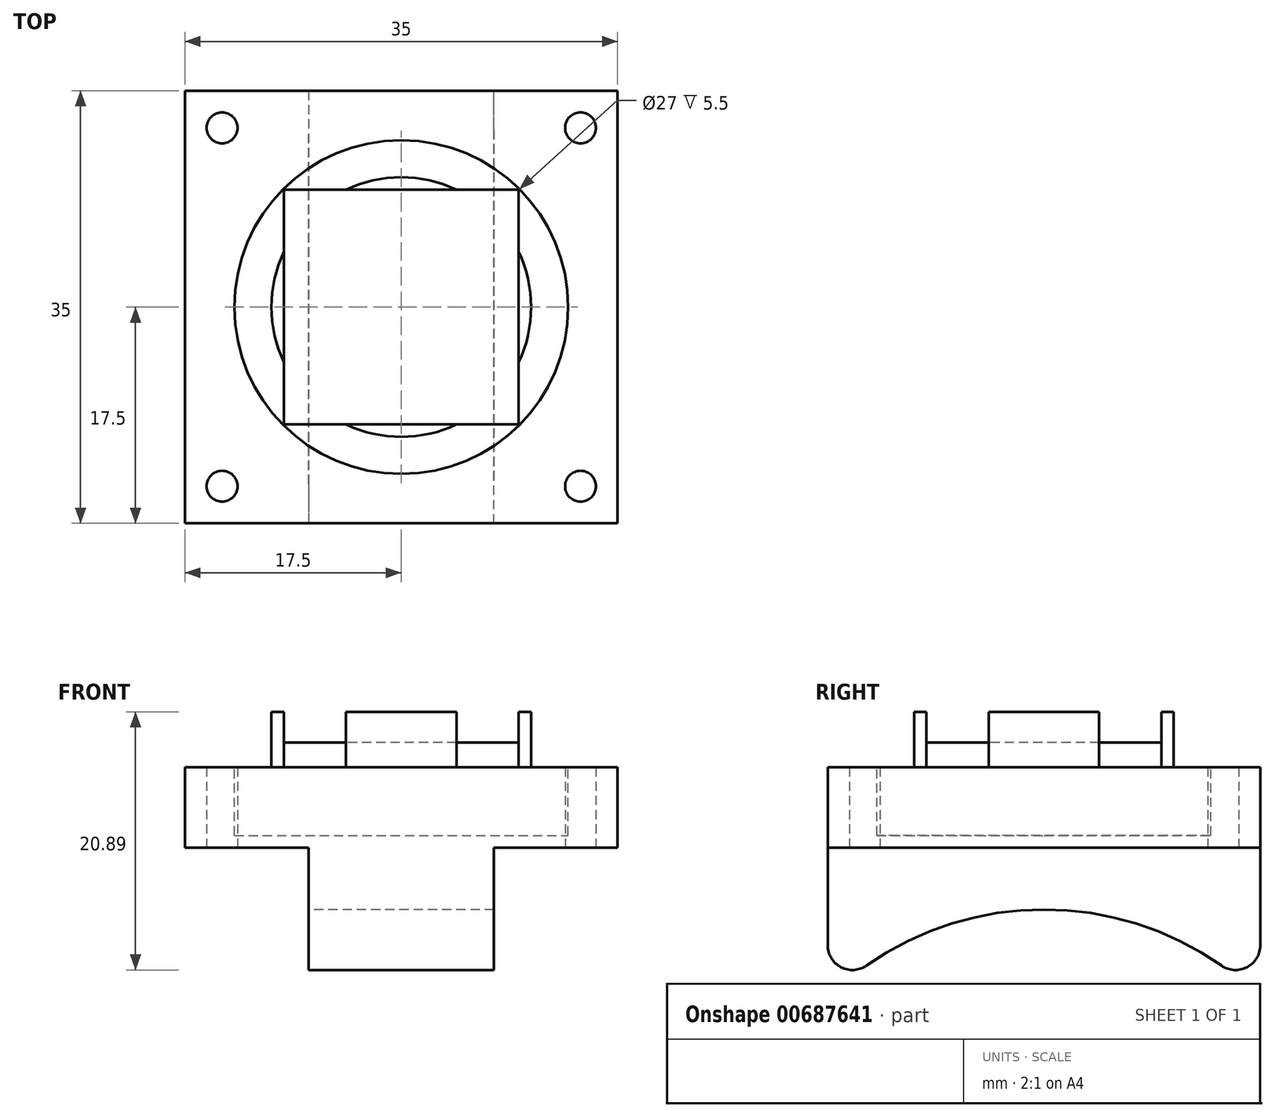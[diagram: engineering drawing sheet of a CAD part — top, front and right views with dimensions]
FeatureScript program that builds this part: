
annotation { "Feature Type Name" : "Feature", "Feature Type Description" : "" }
export const myFeature = defineFeature(function(context is Context, id is Id, definition is map)
    precondition{}
    {
        {
            var Q0;
            Q0=qCreatedBy(makeId("Top.planeOp"),FACE);
            var sketch = newSketch(context, id + "F0", { "sketchPlane" : qUnion([Q0])});
            skLineSegment(sketch, "E0", {"start": v(0, 0) * mm, "end": v(-19, 0) * mm});
            skLineSegment(sketch, "E1", {"start": v(-19, 0) * mm, "end": v(-19, 19) * mm});
            skLineSegment(sketch, "E2", {"start": v(-19, 19) * mm, "end": v(0, 19) * mm});
            skLineSegment(sketch, "E3", {"start": v(0, 19) * mm, "end": v(0, 0) * mm});
            skLineSegment(sketch, "E4.0", {"start": v(2, -2) * mm, "end": v(-21, -2) * mm});
            skLineSegment(sketch, "E4.1", {"start": v(2, 21) * mm, "end": v(2, -2) * mm});
            skLineSegment(sketch, "E4.2", {"start": v(-21, 21) * mm, "end": v(2, 21) * mm});
            skLineSegment(sketch, "E4.3", {"start": v(-21, -2) * mm, "end": v(-21, 21) * mm});
            skCircle(sketch, "E5", {"center": v(-9.5, 9.5) * mm, "radius": 10.5 * mm});
            skPoint(sketch, "E5.centerSnap0", {"position": v(-9.5, 0) * mm});
            skPoint(sketch, "E5.centerSnap1", {"position": v(0, 9.5) * mm});
            skLineSegment(sketch, "E6.0", {"start": v(8, -8) * mm, "end": v(-27, -8) * mm});
            skLineSegment(sketch, "E6.1", {"start": v(8, 27) * mm, "end": v(8, -8) * mm});
            skLineSegment(sketch, "E6.2", {"start": v(-27, 27) * mm, "end": v(8, 27) * mm});
            skLineSegment(sketch, "E6.3", {"start": v(-27, -8) * mm, "end": v(-27, 27) * mm});
            skLineSegment(sketch, "E7", {"start": v(-27, -8) * mm, "end": v(-21, -2) * mm});
            skLineSegment(sketch, "E8", {"start": v(-27, -8) * mm, "end": v(-24, -5) * mm});
            skLineSegment(sketch, "E9", {"start": v(-9.5, 9.5) * mm, "end": v(-11.5, 9.5) * mm});
            skLineSegment(sketch, "E10", {"start": v(-9.5, 9.5) * mm, "end": v(-9.5, 11.53) * mm});
            skLineSegment(sketch, "E11.MirrorCS", {"start": v(-27, 27) * mm, "end": v(-24, 24) * mm});
            skLineSegment(sketch, "E12.MirrorCS", {"start": v(8, -8) * mm, "end": v(5, -5) * mm});
            skLineSegment(sketch, "E13.MirrorCS", {"start": v(8, 27) * mm, "end": v(5, 24) * mm});
            skSolve(sketch);
        }
        {
            var Q0;
            Q0=qSketchRegion(id+"F0",true);
            var Q1;
            {var subQ0=sQuery(id+"F0.wireOp",EDGE,"E5");var subQ1=sQuery(id+"F0.wireOp",EDGE,"E3");var subQ2=makeQuery(id+"F0.imprint","INTERSECT",VERTEX,{"disambiguationData":[OD(0.0)],"derivedFrom":[subQ1,subQ0]});Q1=makeQuery(id+"F0.imprint","IMPRINT",FACE,{"disambiguationData":[TD([[makeQuery(id+"F0.imprint","IMPRINT",EDGE,{"disambiguationData":[TD([[subQ2,-1.0]])],"derivedFrom":subQ1}),1.0]])]});}
            var Q2;
            {var subQ0=sQuery(id+"F0.wireOp",EDGE,"E5");var subQ1=sQuery(id+"F0.wireOp",EDGE,"E0");var subQ2=makeQuery(id+"F0.imprint","INTERSECT",VERTEX,{"disambiguationData":[OD(0.0)],"derivedFrom":[subQ1,subQ0]});Q2=makeQuery(id+"F0.imprint","IMPRINT",FACE,{"disambiguationData":[TD([[makeQuery(id+"F0.imprint","IMPRINT",EDGE,{"disambiguationData":[TD([[subQ2,-1.0]])],"derivedFrom":subQ1}),1.0]])]});}
            var Q3;
            {var subQ0=sQuery(id+"F0.wireOp",EDGE,"E5");var subQ1=sQuery(id+"F0.wireOp",EDGE,"E1");var subQ2=makeQuery(id+"F0.imprint","INTERSECT",VERTEX,{"disambiguationData":[OD(0.0)],"derivedFrom":[subQ1,subQ0]});Q3=makeQuery(id+"F0.imprint","IMPRINT",FACE,{"disambiguationData":[TD([[makeQuery(id+"F0.imprint","IMPRINT",EDGE,{"disambiguationData":[TD([[subQ2,-1.0]])],"derivedFrom":subQ1}),1.0]])]});}
            var Q4;
            {var subQ0=sQuery(id+"F0.wireOp",EDGE,"E5");var subQ1=sQuery(id+"F0.wireOp",EDGE,"E2");var subQ2=makeQuery(id+"F0.imprint","INTERSECT",VERTEX,{"disambiguationData":[OD(0.0)],"derivedFrom":[subQ1,subQ0]});Q4=makeQuery(id+"F0.imprint","IMPRINT",FACE,{"disambiguationData":[TD([[makeQuery(id+"F0.imprint","IMPRINT",EDGE,{"disambiguationData":[TD([[subQ2,-1.0]])],"derivedFrom":subQ1}),1.0]])]});}
            var Q5;
            {var subQ0=sQuery(id+"F0.wireOp",EDGE,"E2");var subQ1=sQuery(id+"F0.wireOp",EDGE,"E1");var subQ2=makeQuery(id+"F0.imprint","INTERSECT",VERTEX,{"derivedFrom":[subQ1,subQ0]});Q5=makeQuery(id+"F0.imprint","IMPRINT",FACE,{"disambiguationData":[TD([[makeQuery(id+"F0.imprint","IMPRINT",EDGE,{"disambiguationData":[TD([[subQ2,1.0]])],"derivedFrom":subQ1}),-1.0]])]});}
            var Q6;
            {var subQ0=sQuery(id+"F0.wireOp",EDGE,"E3");var subQ1=sQuery(id+"F0.wireOp",EDGE,"E2");var subQ2=makeQuery(id+"F0.imprint","INTERSECT",VERTEX,{"derivedFrom":[subQ1,subQ0]});Q6=makeQuery(id+"F0.imprint","IMPRINT",FACE,{"disambiguationData":[TD([[makeQuery(id+"F0.imprint","IMPRINT",EDGE,{"disambiguationData":[TD([[subQ2,1.0]])],"derivedFrom":subQ1}),-1.0]])]});}
            var Q7;
            {var subQ0=sQuery(id+"F0.wireOp",EDGE,"E3");var subQ1=sQuery(id+"F0.wireOp",EDGE,"E0");var subQ2=makeQuery(id+"F0.imprint","INTERSECT",VERTEX,{"derivedFrom":[subQ1,subQ0]});Q7=makeQuery(id+"F0.imprint","IMPRINT",FACE,{"disambiguationData":[TD([[makeQuery(id+"F0.imprint","IMPRINT",EDGE,{"disambiguationData":[TD([[subQ2,-1.0]])],"derivedFrom":subQ1}),-1.0]])]});}
            var Q8;
            {var subQ0=sQuery(id+"F0.wireOp",EDGE,"E1");var subQ1=sQuery(id+"F0.wireOp",EDGE,"E0");var subQ2=makeQuery(id+"F0.imprint","INTERSECT",VERTEX,{"derivedFrom":[subQ1,subQ0]});Q8=makeQuery(id+"F0.imprint","IMPRINT",FACE,{"disambiguationData":[TD([[makeQuery(id+"F0.imprint","IMPRINT",EDGE,{"disambiguationData":[TD([[subQ2,1.0]])],"derivedFrom":subQ1}),-1.0]])]});}
            var Q9;
            Q9=makeQuery(id+"F0.imprint","IMPRINT",FACE,{"disambiguationData":[TD([[makeQuery(id+"F0.imprint","IMPRINT",EDGE,{"derivedFrom":sQuery(id+"F0.wireOp",EDGE,"E4.0")}),-1.0]])]});
            var Q10;
            {var subQ0=sQuery(id+"F0.wireOp",EDGE,"E5");var subQ10=sQuery(id+"F0.wireOp",EDGE,"E0");var subQ11=makeQuery(id+"F0.imprint","INTERSECT",VERTEX,{"disambiguationData":[OD(0.0)],"derivedFrom":[subQ10,subQ0]});Q10=makeQuery(id+"F0.imprint","IMPRINT",FACE,{"disambiguationData":[TD([[makeQuery(id+"F0.imprint","IMPRINT",EDGE,{"disambiguationData":[TD([[subQ11,-1.0]])],"derivedFrom":subQ10}),-1.0]])]});}
            extrude(context, id + "F1", {"entities" : qUnion([Q0, Q1, Q2, Q3, Q4, Q5, Q6, Q7, Q8, Q9, Q10]), "oppositeDirection" : true, "depth" : 2 * mm, "offsetDistance" : 25 * mm});
        }
        {
            var Q0;
            Q0=makeQuery(id+"F1.opExtrude","CAP_FACE",FACE,{"disambiguationData":[OSD([sQuery(id+"F0.wireOp",EDGE,"E6.0"),sQuery(id+"F0.wireOp",EDGE,"E6.1"),sQuery(id+"F0.wireOp",EDGE,"E6.2"),sQuery(id+"F0.wireOp",EDGE,"E6.3")])],"isStart":false});
            var sketch = newSketch(context, id + "F2", { "sketchPlane" : qUnion([Q0])});
            skLineSegment(sketch, "E14", {"start": v(-27, -27) * mm, "end": v(-27, 8) * mm});
            skLineSegment(sketch, "E15", {"start": v(-27, 8) * mm, "end": v(8, 8) * mm});
            skLineSegment(sketch, "E16", {"start": v(8, 8) * mm, "end": v(8, -27) * mm});
            skLineSegment(sketch, "E17", {"start": v(8, -27) * mm, "end": v(-27, -27) * mm});
            skLineSegment(sketch, "E18", {"start": v(-27, -9.5) * mm, "end": v(8, -9.5) * mm});
            skCircle(sketch, "E19", {"center": v(-9.5, -9.5) * mm, "radius": 13.5 * mm});
            skSolve(sketch);
        }
        {
            var Q0;
            Q0=qSketchRegion(id+"F2",true);
            extrude(context, id + "F3", {"entities" : qUnion([Q0]), "depth" : 5.5 * mm, "offsetDistance" : 25 * mm});
        }
        {
            var Q0;
            {var subQ0=sQuery(id+"F0.wireOp",EDGE,"E5");var subQ1=sQuery(id+"F0.wireOp",EDGE,"E1");var subQ2=makeQuery(id+"F0.imprint","INTERSECT",VERTEX,{"disambiguationData":[OD(0.0)],"derivedFrom":[subQ1,subQ0]});Q0=makeQuery(id+"F0.imprint","IMPRINT",FACE,{"disambiguationData":[TD([[makeQuery(id+"F0.imprint","IMPRINT",EDGE,{"disambiguationData":[TD([[subQ2,-1.0]])],"derivedFrom":subQ1}),1.0]])]});}
            var Q1;
            {var subQ0=sQuery(id+"F0.wireOp",EDGE,"E5");var subQ1=sQuery(id+"F0.wireOp",EDGE,"E2");var subQ2=makeQuery(id+"F0.imprint","INTERSECT",VERTEX,{"disambiguationData":[OD(0.0)],"derivedFrom":[subQ1,subQ0]});Q1=makeQuery(id+"F0.imprint","IMPRINT",FACE,{"disambiguationData":[TD([[makeQuery(id+"F0.imprint","IMPRINT",EDGE,{"disambiguationData":[TD([[subQ2,-1.0]])],"derivedFrom":subQ1}),1.0]])]});}
            var Q2;
            {var subQ0=sQuery(id+"F0.wireOp",EDGE,"E5");var subQ1=sQuery(id+"F0.wireOp",EDGE,"E3");var subQ2=makeQuery(id+"F0.imprint","INTERSECT",VERTEX,{"disambiguationData":[OD(0.0)],"derivedFrom":[subQ1,subQ0]});Q2=makeQuery(id+"F0.imprint","IMPRINT",FACE,{"disambiguationData":[TD([[makeQuery(id+"F0.imprint","IMPRINT",EDGE,{"disambiguationData":[TD([[subQ2,-1.0]])],"derivedFrom":subQ1}),1.0]])]});}
            var Q3;
            {var subQ0=sQuery(id+"F0.wireOp",EDGE,"E5");var subQ1=sQuery(id+"F0.wireOp",EDGE,"E0");var subQ2=makeQuery(id+"F0.imprint","INTERSECT",VERTEX,{"disambiguationData":[OD(0.0)],"derivedFrom":[subQ1,subQ0]});Q3=makeQuery(id+"F0.imprint","IMPRINT",FACE,{"disambiguationData":[TD([[makeQuery(id+"F0.imprint","IMPRINT",EDGE,{"disambiguationData":[TD([[subQ2,-1.0]])],"derivedFrom":subQ1}),1.0]])]});}
            var Q4;
            Q4=makeQuery(id+"F0.imprint","IMPRINT",FACE,{"disambiguationData":[TD([[makeQuery(id+"F0.imprint","IMPRINT",EDGE,{"derivedFrom":sQuery(id+"F0.wireOp",EDGE,"E4.0")}),-1.0]])]});
            extrude(context, id + "F4", {"entities" : qUnion([Q0, Q1, Q2, Q3, Q4]), "operationType" : NewBodyOperationType.ADD, "depth" : 2.5 * mm, "offsetDistance" : 25 * mm});
        }
        {
            var Q0;
            Q0=makeQuery(id+"F3.opExtrude","CAP_FACE",FACE,{"disambiguationData":[OSD([sQuery(id+"F2.wireOp",EDGE,"E14"),sQuery(id+"F2.wireOp",EDGE,"E15"),sQuery(id+"F2.wireOp",EDGE,"E16"),sQuery(id+"F2.wireOp",EDGE,"E17"),sQuery(id+"F2.wireOp",EDGE,"E19")])],"isStart":false});
            var Q1;
            Q1=makeQuery(id+"F1.opExtrude","CAP_FACE",FACE,{"disambiguationData":[OSD([sQuery(id+"F0.wireOp",EDGE,"E6.0"),sQuery(id+"F0.wireOp",EDGE,"E6.1"),sQuery(id+"F0.wireOp",EDGE,"E6.2"),sQuery(id+"F0.wireOp",EDGE,"E6.3")])],"isStart":false});
            extrude(context, id + "F5", {"entities" : qUnion([Q0, Q1]), "depth" : 1 * mm, "offsetDistance" : 25 * mm});
        }
        {
            var Q0;
            Q0=makeQuery(id+"F5.opExtrude","SWEPT_BODY",BODY,{"disambiguationData":[OSD([sQuery(id+"F2.wireOp",EDGE,"E14"),sQuery(id+"F2.wireOp",EDGE,"E15"),sQuery(id+"F2.wireOp",EDGE,"E16"),sQuery(id+"F2.wireOp",EDGE,"E17"),sQuery(id+"F2.wireOp",EDGE,"E19")])]});
            var Q1;
            Q1=makeQuery(id+"F5.opExtrude","SWEPT_BODY",BODY,{"disambiguationData":[OSD([sQuery(id+"F0.wireOp",EDGE,"E6.0"),sQuery(id+"F0.wireOp",EDGE,"E6.1"),sQuery(id+"F0.wireOp",EDGE,"E6.2"),sQuery(id+"F0.wireOp",EDGE,"E6.3")])]});
            deleteBodies(context, id + "F6", {"entities" : qUnion([Q0, Q1])});
        }
        {
            var Q0;
            Q0=makeQuery(id+"F3.opExtrude","CAP_FACE",FACE,{"disambiguationData":[OSD([sQuery(id+"F2.wireOp",EDGE,"E14"),sQuery(id+"F2.wireOp",EDGE,"E15"),sQuery(id+"F2.wireOp",EDGE,"E16"),sQuery(id+"F2.wireOp",EDGE,"E17"),sQuery(id+"F2.wireOp",EDGE,"E19")])],"isStart":false});
            var sketch = newSketch(context, id + "F7", { "sketchPlane" : qUnion([Q0])});
            skLineSegment(sketch, "E20", {"start": v(-27, -27) * mm, "end": v(8, -27) * mm});
            skLineSegment(sketch, "E21", {"start": v(8, -27) * mm, "end": v(8, 8) * mm});
            skLineSegment(sketch, "E22", {"start": v(8, 8) * mm, "end": v(-27, 8) * mm});
            skLineSegment(sketch, "E23", {"start": v(-27, 8) * mm, "end": v(-27, -27) * mm});
            skSolve(sketch);
        }
        {
            var Q0;
            Q0=makeQuery(id+"F7.imprint","IMPRINT",FACE,{"disambiguationData":[TD([[makeQuery(id+"F7.imprint","IMPRINT",EDGE,{"derivedFrom":sQuery(id+"F7.wireOp",EDGE,"E20")}),1.0]])]});
            var Q1;
            Q1=makeQuery(id+"F7.imprint","IMPRINT",FACE,{"disambiguationData":[TD([[makeQuery(id+"F7.imprint","IMPRINT",EDGE,{"derivedFrom":makeQuery(id+"FP3SZp29wrBzVes_1.hole-0.boolean.opBoolean","INTERSECT",EDGE,{"derivedFrom":[makeQuery(id+"F3.opExtrude","CAP_FACE",FACE,{"disambiguationData":[OSD([sQuery(id+"F2.wireOp",EDGE,"E14"),sQuery(id+"F2.wireOp",EDGE,"E15"),sQuery(id+"F2.wireOp",EDGE,"E16"),sQuery(id+"F2.wireOp",EDGE,"E17"),sQuery(id+"F2.wireOp",EDGE,"E19")])],"isStart":false}),makeQuery(id+"FP3SZp29wrBzVes_1.hole-0.opRevolve","SWEPT_FACE",FACE,{"disambiguationData":[OSD([sQuery(id+"FP3SZp29wrBzVes_1.hole-0.sketch.wireOp",EDGE,"core_line_2")])]})]})}),-1.0]])]});
            var Q2;
            Q2=makeQuery(id+"F7.imprint","IMPRINT",FACE,{"disambiguationData":[TD([[makeQuery(id+"F7.imprint","IMPRINT",EDGE,{"derivedFrom":makeQuery(id+"FP3SZp29wrBzVes_1.hole-1.boolean.opBoolean","INTERSECT",EDGE,{"derivedFrom":[makeQuery(id+"F3.opExtrude","CAP_FACE",FACE,{"disambiguationData":[OSD([sQuery(id+"F2.wireOp",EDGE,"E14"),sQuery(id+"F2.wireOp",EDGE,"E15"),sQuery(id+"F2.wireOp",EDGE,"E16"),sQuery(id+"F2.wireOp",EDGE,"E17"),sQuery(id+"F2.wireOp",EDGE,"E19")])],"isStart":false}),makeQuery(id+"FP3SZp29wrBzVes_1.hole-1.opRevolve","SWEPT_FACE",FACE,{"disambiguationData":[OSD([sQuery(id+"FP3SZp29wrBzVes_1.hole-1.sketch.wireOp",EDGE,"core_line_2")])]})]})}),-1.0]])]});
            var Q3;
            Q3=makeQuery(id+"F7.imprint","IMPRINT",FACE,{"disambiguationData":[TD([[makeQuery(id+"F7.imprint","IMPRINT",EDGE,{"derivedFrom":makeQuery(id+"FP3SZp29wrBzVes_1.hole-3.boolean.opBoolean","INTERSECT",EDGE,{"derivedFrom":[makeQuery(id+"F3.opExtrude","CAP_FACE",FACE,{"disambiguationData":[OSD([sQuery(id+"F2.wireOp",EDGE,"E14"),sQuery(id+"F2.wireOp",EDGE,"E15"),sQuery(id+"F2.wireOp",EDGE,"E16"),sQuery(id+"F2.wireOp",EDGE,"E17"),sQuery(id+"F2.wireOp",EDGE,"E19")])],"isStart":false}),makeQuery(id+"FP3SZp29wrBzVes_1.hole-3.opRevolve","SWEPT_FACE",FACE,{"disambiguationData":[OSD([sQuery(id+"FP3SZp29wrBzVes_1.hole-3.sketch.wireOp",EDGE,"core_line_2")])]})]})}),-1.0]])]});
            var Q4;
            Q4=makeQuery(id+"F7.imprint","IMPRINT",FACE,{"disambiguationData":[TD([[makeQuery(id+"F7.imprint","IMPRINT",EDGE,{"derivedFrom":makeQuery(id+"F3.opExtrude","CAP_EDGE",EDGE,{"disambiguationData":[OSD([sQuery(id+"F2.wireOp",EDGE,"E19")])],"isStart":false})}),1.0]])]});
            var Q5;
            Q5=makeQuery(id+"F7.imprint","IMPRINT",FACE,{"disambiguationData":[TD([[makeQuery(id+"F7.imprint","IMPRINT",EDGE,{"derivedFrom":makeQuery(id+"FP3SZp29wrBzVes_1.hole-2.boolean.opBoolean","INTERSECT",EDGE,{"derivedFrom":[makeQuery(id+"F3.opExtrude","CAP_FACE",FACE,{"disambiguationData":[OSD([sQuery(id+"F2.wireOp",EDGE,"E14"),sQuery(id+"F2.wireOp",EDGE,"E15"),sQuery(id+"F2.wireOp",EDGE,"E16"),sQuery(id+"F2.wireOp",EDGE,"E17"),sQuery(id+"F2.wireOp",EDGE,"E19")])],"isStart":false}),makeQuery(id+"FP3SZp29wrBzVes_1.hole-2.opRevolve","SWEPT_FACE",FACE,{"disambiguationData":[OSD([sQuery(id+"FP3SZp29wrBzVes_1.hole-2.sketch.wireOp",EDGE,"core_line_2")])]})]})}),-1.0]])]});
            extrude(context, id + "F8", {"entities" : qUnion([Q0, Q1, Q2, Q3, Q4, Q5]), "operationType" : NewBodyOperationType.ADD, "depth" : 1 * mm, "offsetDistance" : 25 * mm});
        }
        {
            var Q0;
            Q0=sQuery(id+"F0.wireOp",VERTEX,"E8.end");
            var Q1;
            Q1=sQuery(id+"F0.wireOp",VERTEX,"E11.MirrorCS.end");
            var Q2;
            Q2=sQuery(id+"F0.wireOp",VERTEX,"E13.MirrorCS.end");
            var Q3;
            Q3=sQuery(id+"F0.wireOp",VERTEX,"E12.MirrorCS.end");
            var Q4;
            Q4=makeQuery(id+"F3.opExtrude","SWEPT_BODY",BODY,{"disambiguationData":[OSD([sQuery(id+"F2.wireOp",EDGE,"E14"),sQuery(id+"F2.wireOp",EDGE,"E15"),sQuery(id+"F2.wireOp",EDGE,"E16"),sQuery(id+"F2.wireOp",EDGE,"E17"),sQuery(id+"F2.wireOp",EDGE,"E19")])]});
            var Q5;
            Q5=makeQuery(id+"F1.opExtrude","SWEPT_BODY",BODY,{"disambiguationData":[OSD([sQuery(id+"F0.wireOp",EDGE,"E6.0"),sQuery(id+"F0.wireOp",EDGE,"E6.1"),sQuery(id+"F0.wireOp",EDGE,"E6.2"),sQuery(id+"F0.wireOp",EDGE,"E6.3")])]});
            hole(context, id + "F9", {"style" : HoleStyle.SIMPLE, "endStyle" : HoleEndStyle.BLIND, "holeDiameter" : 2.5 * mm, "majorDiameter" : 5 * mm, "holeDepth" : 10 * mm, "isTappedThrough" : true, "tappedDepth" : 12 * mm, "tapClearance" : 3, "locations" : qUnion([Q0, Q1, Q2, Q3]), "scope" : qUnion([Q4, Q5]), "startStyle" : HoleStartStyle.PART});
        }
        {
            var Q0;
            Q0=makeQuery(id+"F8.opExtrude","CAP_FACE",FACE,{"disambiguationData":[OSD([sQuery(id+"F7.wireOp",EDGE,"E20"),sQuery(id+"F7.wireOp",EDGE,"E21"),sQuery(id+"F7.wireOp",EDGE,"E22"),sQuery(id+"F7.wireOp",EDGE,"E23")])],"isStart":false});
            var sketch = newSketch(context, id + "F10", { "sketchPlane" : qUnion([Q0])});
            skLineSegment(sketch, "E24", {"start": v(-27, 8) * mm, "end": v(8, 8) * mm});
            skLineSegment(sketch, "E25", {"start": v(8, 8) * mm, "end": v(8, -27) * mm});
            skLineSegment(sketch, "E26", {"start": v(8, -27) * mm, "end": v(-27, -27) * mm});
            skLineSegment(sketch, "E27", {"start": v(-27, -27) * mm, "end": v(-27, 8) * mm});
            skLineSegment(sketch, "E28", {"start": v(-9.5, 8) * mm, "end": v(-9.5, -27) * mm});
            skLineSegment(sketch, "E29", {"start": v(-9.5, -9.5) * mm, "end": v(-17, -9.5) * mm});
            skLineSegment(sketch, "E30", {"start": v(-17, -9.5) * mm, "end": v(-17, 8) * mm});
            skLineSegment(sketch, "E31.MirrorCS", {"start": v(-2, -9.5) * mm, "end": v(-2, 8) * mm});
            skLineSegment(sketch, "E32.MirrorCS", {"start": v(-17, -9.5) * mm, "end": v(-17, -27) * mm});
            skLineSegment(sketch, "E33.MirrorCS", {"start": v(-2, -9.5) * mm, "end": v(-2, -27) * mm});
            skSolve(sketch);
        }
        {
            var Q0;
            {var subQ4=sQuery(id+"F10.wireOp",EDGE,"E29");Q0=makeQuery(id+"F10.imprint","IMPRINT",FACE,{"disambiguationData":[TD([[makeQuery(id+"F10.imprint","IMPRINT",EDGE,{"derivedFrom":subQ4}),-1.0]])]});}
            var Q1;
            {var subQ4=sQuery(id+"F10.wireOp",EDGE,"E29");Q1=makeQuery(id+"F10.imprint","IMPRINT",FACE,{"disambiguationData":[TD([[makeQuery(id+"F10.imprint","IMPRINT",EDGE,{"derivedFrom":subQ4}),1.0]])]});}
            var Q2;
            {var subQ7=sQuery(id+"F10.wireOp",EDGE,"E31.MirrorCS");Q2=makeQuery(id+"F10.imprint","IMPRINT",FACE,{"disambiguationData":[TD([[makeQuery(id+"F10.imprint","IMPRINT",EDGE,{"derivedFrom":subQ7}),1.0]])]});}
            extrude(context, id + "F11", {"entities" : qUnion([Q0, Q1, Q2]), "operationType" : NewBodyOperationType.ADD, "depth" : 25 * mm, "offsetDistance" : 25 * mm});
        }
        {
            var Q0;
            Q0=makeQuery(id+"F11.opExtrude","SWEPT_FACE",FACE,{"disambiguationData":[OSD([sQuery(id+"F10.wireOp",EDGE,"E30"),sQuery(id+"F10.wireOp",EDGE,"E32.MirrorCS")])]});
            var sketch = newSketch(context, id + "F12", { "sketchPlane" : qUnion([Q0])});
            skLineSegment(sketch, "E34", {"start": v(-9.5, -33.5) * mm, "end": v(-9.5, -38.5) * mm});
            skCircle(sketch, "E35", {"center": v(-9.5, -38.5) * mm, "radius": 25 * mm});
            skSolve(sketch);
        }
        {
            var Q0;
            Q0=qSketchRegion(id+"F12",true);
            extrude(context, id + "F13", {"entities" : qUnion([Q0]), "operationType" : NewBodyOperationType.REMOVE, "oppositeDirection" : true, "depth" : 25 * mm, "offsetDistance" : 25 * mm});
        }
        {
            var Q0;
            Q0=makeQuery(id+"F13.boolean.opBoolean","INTERSECT",EDGE,{"derivedFrom":[makeQuery(id+"F11.boolean.opBoolean","MERGE",FACE,{"derivedFrom":[makeQuery(id+"F8.boolean.opBoolean","MERGE",FACE,{"derivedFrom":[makeQuery(id+"F3.opExtrude","SWEPT_FACE",FACE,{"disambiguationData":[OSD([sQuery(id+"F2.wireOp",EDGE,"E15")])]}),makeQuery(id+"F8.opExtrude","SWEPT_FACE",FACE,{"disambiguationData":[OSD([sQuery(id+"F7.wireOp",EDGE,"E22")])]})]}),makeQuery(id+"F11.opExtrude","SWEPT_FACE",FACE,{"disambiguationData":[OSD([sQuery(id+"F10.wireOp",EDGE,"E24")])]})]}),makeQuery(id+"F13.opExtrude","SWEPT_FACE",FACE,{"disambiguationData":[OSD([sQuery(id+"F12.wireOp",EDGE,"E35")])]})]});
            var Q1;
            Q1=makeQuery(id+"F13.boolean.opBoolean","INTERSECT",EDGE,{"derivedFrom":[makeQuery(id+"F11.boolean.opBoolean","MERGE",FACE,{"derivedFrom":[makeQuery(id+"F8.boolean.opBoolean","MERGE",FACE,{"derivedFrom":[makeQuery(id+"F3.opExtrude","SWEPT_FACE",FACE,{"disambiguationData":[OSD([sQuery(id+"F2.wireOp",EDGE,"E17")])]}),makeQuery(id+"F8.opExtrude","SWEPT_FACE",FACE,{"disambiguationData":[OSD([sQuery(id+"F7.wireOp",EDGE,"E20")])]})]}),makeQuery(id+"F11.opExtrude","SWEPT_FACE",FACE,{"disambiguationData":[OSD([sQuery(id+"F10.wireOp",EDGE,"E26")])]})]}),makeQuery(id+"F13.opExtrude","SWEPT_FACE",FACE,{"disambiguationData":[OSD([sQuery(id+"F12.wireOp",EDGE,"E35")])]})]});
            fillet(context, id + "F14", {"entities" : qUnion([Q0, Q1]), "radius" : 2 * mm, "tangentPropagation" : true, "allowEdgeOverflow" : false});
        }
        {
            var Q0;
            Q0=makeQuery(id+"F1.opExtrude","SWEPT_BODY",BODY,{"disambiguationData":[OSD([sQuery(id+"F0.wireOp",EDGE,"E6.0"),sQuery(id+"F0.wireOp",EDGE,"E6.1"),sQuery(id+"F0.wireOp",EDGE,"E6.2"),sQuery(id+"F0.wireOp",EDGE,"E6.3")])]});
            deleteBodies(context, id + "F15", {"entities" : qUnion([Q0])});
        }
    });
